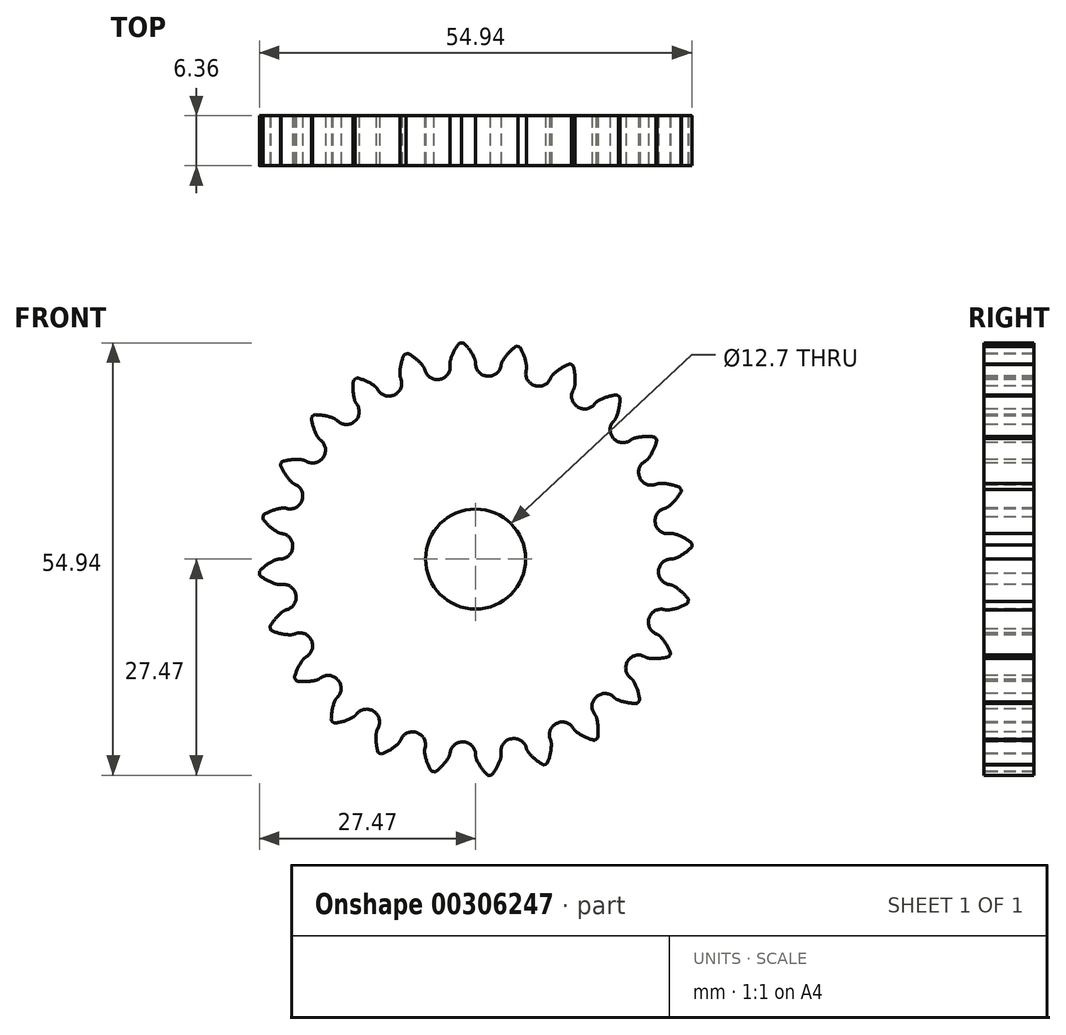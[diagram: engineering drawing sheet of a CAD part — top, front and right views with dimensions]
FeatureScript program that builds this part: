
annotation { "Feature Type Name" : "Feature", "Feature Type Description" : "" }
export const myFeature = defineFeature(function(context is Context, id is Id, definition is map)
    precondition{}
    {
        {
            var Q0;
            Q0=qCreatedBy(makeId("Front.planeOp"),FACE);
            var sketch = newSketch(context, id + "F0", { "sketchPlane" : qUnion([Q0])});
            skCircle(sketch, "E0", {"center": v(0, 0) * mm, "radius": 23.28 * mm});
            skSolve(sketch);
        }
        {
            var Q0;
            Q0=qSketchRegion(id+"F0",true);
            extrude(context, id + "F1", {"entities" : qUnion([Q0]), "depth" : 3.17 * mm});
        }
        {
            var Q0;
            Q0=makeQuery(id+"F1.opExtrude","CAP_FACE",FACE,{"disambiguationData":[OSD([sQuery(id+"F0.wireOp",EDGE,"E0")])],"isStart":true});
            extrude(context, id + "F2", {"entities" : qUnion([Q0]), "operationType" : NewBodyOperationType.ADD, "depth" : 3.17 * mm});
        }
        {
            var Q0;
            Q0=makeQuery(id+"F1.opExtrude","CAP_FACE",FACE,{"disambiguationData":[OSD([sQuery(id+"F0.wireOp",EDGE,"E0")])],"isStart":false});
            var sketch = newSketch(context, id + "F3", { "sketchPlane" : qUnion([Q0])});
            skArc(sketch, "E1.trimOffspring", {"start": v(-0.14, 25.48) * mm, "mid": v(-0.74, 26.53) * mm, "end": v(-1.53, 27.45) * mm});
            skLineSegment(sketch, "E2", {"start": v(-1.58, 27.47) * mm, "end": v(-1.8, 27.47) * mm});
            skLineSegment(sketch, "E3", {"start": v(0, 24.83) * mm, "end": v(0, 24.82) * mm});
            skLineSegment(sketch, "E4.MirrorCS", {"start": v(-2.01, 27.44) * mm, "end": v(-1.8, 27.47) * mm});
            skArc(sketch, "E5.MirrorCS", {"start": v(-3.19, 25.28) * mm, "mid": v(-2.73, 26.4) * mm, "end": v(-2.07, 27.41) * mm});
            skLineSegment(sketch, "E6.MirrorCS", {"start": v(-3.24, 24.62) * mm, "end": v(-3.24, 24.6) * mm});
            skArc(sketch, "E7.filletArc", {"start": v(-3.21, 23.06) * mm, "mid": v(-3.1, 23.13) * mm, "end": v(-3.06, 23.26) * mm});
            skArc(sketch, "E8.filletArc", {"start": v(-4.5, 22.84) * mm, "mid": v(-3.52, 23.47) * mm, "end": v(-3.24, 24.6) * mm});
            skArc(sketch, "E9.filletArc", {"start": v(0, 24.82) * mm, "mid": v(0.43, 23.73) * mm, "end": v(1.49, 23.24) * mm});
            skPoint(sketch, "E10.visualSharp", {"position": v(0, 25.15) * mm});
            skArc(sketch, "E10.filletArc", {"start": v(0, 24.83) * mm, "mid": v(-0.04, 25.16) * mm, "end": v(-0.14, 25.48) * mm});
            skPoint(sketch, "E11.visualSharp", {"position": v(-3.28, 24.93) * mm});
            skArc(sketch, "E11.filletArc", {"start": v(-3.19, 25.28) * mm, "mid": v(-3.25, 24.95) * mm, "end": v(-3.24, 24.62) * mm});
            skPoint(sketch, "E12.visualSharp", {"position": v(-2.05, 27.44) * mm});
            skArc(sketch, "E13.filletArc", {"start": v(-2.01, 27.44) * mm, "mid": v(-2.04, 27.43) * mm, "end": v(-2.07, 27.41) * mm});
            skPoint(sketch, "E14.visualSharp", {"position": v(-1.55, 27.47) * mm});
            skArc(sketch, "E14.filletArc", {"start": v(-1.53, 27.45) * mm, "mid": v(-1.55, 27.47) * mm, "end": v(-1.58, 27.47) * mm});
            skArc(sketch, "E15.1.0", {"start": v(-9.62, 23.6) * mm, "mid": v(-9.47, 24.8) * mm, "end": v(-9.1, 25.94) * mm});
            skArc(sketch, "E15.1.1", {"start": v(-6.42, 23.97) * mm, "mid": v(-5.73, 23.04) * mm, "end": v(-4.58, 22.83) * mm});
            skArc(sketch, "E15.1.2", {"start": v(-6.73, 24.58) * mm, "mid": v(-7.58, 25.44) * mm, "end": v(-8.58, 26.12) * mm});
            skPoint(sketch, "E15.1.3", {"position": v(-6.5, 24.29) * mm});
            skPoint(sketch, "E15.1.4", {"position": v(-9.62, 23.23) * mm});
            skPoint(sketch, "E15.1.5", {"position": v(-9.08, 25.98) * mm});
            skPoint(sketch, "E15.1.6", {"position": v(-8.6, 26.14) * mm});
            skArc(sketch, "E15.1.7", {"start": v(-10.27, 20.9) * mm, "mid": v(-9.48, 21.76) * mm, "end": v(-9.5, 22.93) * mm});
            skArc(sketch, "E15.1.8", {"start": v(-9.07, 21.44) * mm, "mid": v(-8.98, 21.54) * mm, "end": v(-8.98, 21.67) * mm});
            skArc(sketch, "E15.1.9", {"start": v(-6.43, 23.98) * mm, "mid": v(-6.55, 24.3) * mm, "end": v(-6.73, 24.58) * mm});
            skArc(sketch, "E15.1.10", {"start": v(-9.62, 23.6) * mm, "mid": v(-9.6, 23.26) * mm, "end": v(-9.5, 22.94) * mm});
            skLineSegment(sketch, "E15.1.11", {"start": v(-9.5, 22.94) * mm, "end": v(-9.5, 22.93) * mm});
            skLineSegment(sketch, "E15.1.12", {"start": v(-6.43, 23.98) * mm, "end": v(-6.42, 23.97) * mm});
            skLineSegment(sketch, "E15.1.13", {"start": v(-9.05, 25.99) * mm, "end": v(-8.85, 26.07) * mm});
            skArc(sketch, "E15.1.14", {"start": v(-9.05, 25.99) * mm, "mid": v(-9.08, 25.97) * mm, "end": v(-9.1, 25.94) * mm});
            skArc(sketch, "E15.1.15", {"start": v(-8.58, 26.12) * mm, "mid": v(-8.6, 26.13) * mm, "end": v(-8.64, 26.13) * mm});
            skLineSegment(sketch, "E15.1.16", {"start": v(-8.64, 26.13) * mm, "end": v(-8.85, 26.07) * mm});
            skArc(sketch, "E15.2.0", {"start": v(-15.4, 20.3) * mm, "mid": v(-15.57, 21.5) * mm, "end": v(-15.5, 22.7) * mm});
            skArc(sketch, "E15.2.1", {"start": v(-12.41, 21.5) * mm, "mid": v(-11.5, 20.77) * mm, "end": v(-10.33, 20.87) * mm});
            skArc(sketch, "E15.2.2", {"start": v(-12.86, 22) * mm, "mid": v(-13.9, 22.6) * mm, "end": v(-15.05, 23) * mm});
            skPoint(sketch, "E15.2.3", {"position": v(-12.57, 21.78) * mm});
            skPoint(sketch, "E15.2.4", {"position": v(-15.3, 19.95) * mm});
            skPoint(sketch, "E15.2.5", {"position": v(-15.5, 22.74) * mm});
            skPoint(sketch, "E15.2.6", {"position": v(-15.08, 23.02) * mm});
            skArc(sketch, "E15.2.7", {"start": v(-15.32, 17.53) * mm, "mid": v(-14.79, 18.57) * mm, "end": v(-15.1, 19.7) * mm});
            skArc(sketch, "E15.2.8", {"start": v(-14.31, 18.36) * mm, "mid": v(-14.25, 18.48) * mm, "end": v(-14.28, 18.61) * mm});
            skArc(sketch, "E15.2.9", {"start": v(-12.42, 21.5) * mm, "mid": v(-12.61, 21.77) * mm, "end": v(-12.86, 22) * mm});
            skArc(sketch, "E15.2.10", {"start": v(-15.4, 20.3) * mm, "mid": v(-15.3, 19.99) * mm, "end": v(-15.12, 19.7) * mm});
            skLineSegment(sketch, "E15.2.11", {"start": v(-15.12, 19.7) * mm, "end": v(-15.1, 19.7) * mm});
            skLineSegment(sketch, "E15.2.12", {"start": v(-12.42, 21.5) * mm, "end": v(-12.41, 21.5) * mm});
            skLineSegment(sketch, "E15.2.13", {"start": v(-15.47, 22.76) * mm, "end": v(-15.3, 22.9) * mm});
            skArc(sketch, "E15.2.14", {"start": v(-15.47, 22.76) * mm, "mid": v(-15.49, 22.74) * mm, "end": v(-15.5, 22.7) * mm});
            skArc(sketch, "E15.2.15", {"start": v(-15.05, 23) * mm, "mid": v(-15.08, 23.01) * mm, "end": v(-15.1, 23) * mm});
            skLineSegment(sketch, "E15.2.16", {"start": v(-15.1, 23) * mm, "end": v(-15.3, 22.9) * mm});
            skPoint(sketch, "E15.center", {"position": v(0, 0) * mm});
            skArc(sketch, "E16.4.3.0", {"start": v(-17.55, 17.55) * mm, "mid": v(-16.48, 17.09) * mm, "end": v(-15.38, 17.48) * mm});
            skArc(sketch, "E16.8.3.0", {"start": v(-18.12, 17.92) * mm, "mid": v(-19.29, 18.24) * mm, "end": v(-20.5, 18.33) * mm});
            skArc(sketch, "E16.9.3.0", {"start": v(-20.13, 15.62) * mm, "mid": v(-20.6, 16.74) * mm, "end": v(-20.85, 17.92) * mm});
            skPoint(sketch, "E16.12.3.0", {"position": v(-17.78, 17.78) * mm});
            skPoint(sketch, "E16.13.3.0", {"position": v(-19.95, 15.3) * mm});
            skPoint(sketch, "E16.14.3.0", {"position": v(-20.85, 17.96) * mm});
            skPoint(sketch, "E16.15.3.0", {"position": v(-20.52, 18.33) * mm});
            skArc(sketch, "E16.16.3.0", {"start": v(-19.34, 12.97) * mm, "mid": v(-19.1, 14.1) * mm, "end": v(-19.7, 15.1) * mm});
            skArc(sketch, "E16.20.3.0", {"start": v(-18.58, 14.03) * mm, "mid": v(-18.54, 14.16) * mm, "end": v(-18.61, 14.28) * mm});
            skArc(sketch, "E16.24.3.0", {"start": v(-17.56, 17.56) * mm, "mid": v(-17.82, 17.77) * mm, "end": v(-18.12, 17.92) * mm});
            skArc(sketch, "E16.28.3.0", {"start": v(-20.13, 15.62) * mm, "mid": v(-19.94, 15.35) * mm, "end": v(-19.7, 15.12) * mm});
            skLineSegment(sketch, "E16.32.3.0", {"start": v(-19.7, 15.12) * mm, "end": v(-19.7, 15.1) * mm});
            skLineSegment(sketch, "E16.35.3.0", {"start": v(-17.56, 17.56) * mm, "end": v(-17.55, 17.55) * mm});
            skLineSegment(sketch, "E16.38.3.0", {"start": v(-20.83, 17.98) * mm, "end": v(-20.7, 18.15) * mm});
            skArc(sketch, "E16.41.3.0", {"start": v(-20.83, 17.98) * mm, "mid": v(-20.85, 17.95) * mm, "end": v(-20.85, 17.92) * mm});
            skArc(sketch, "E16.45.3.0", {"start": v(-20.5, 18.33) * mm, "mid": v(-20.52, 18.32) * mm, "end": v(-20.54, 18.3) * mm});
            skLineSegment(sketch, "E16.49.3.0", {"start": v(-20.54, 18.3) * mm, "end": v(-20.7, 18.15) * mm});
            skArc(sketch, "E16.4.4.0", {"start": v(-21.5, 12.41) * mm, "mid": v(-20.34, 12.24) * mm, "end": v(-19.38, 12.9) * mm});
            skArc(sketch, "E16.8.4.0", {"start": v(-22.14, 12.62) * mm, "mid": v(-23.35, 12.63) * mm, "end": v(-24.54, 12.4) * mm});
            skArc(sketch, "E16.9.4.0", {"start": v(-23.49, 9.88) * mm, "mid": v(-24.23, 10.84) * mm, "end": v(-24.78, 11.92) * mm});
            skPoint(sketch, "E16.12.4.0", {"position": v(-21.78, 12.57) * mm});
            skPoint(sketch, "E16.13.4.0", {"position": v(-23.23, 9.62) * mm});
            skPoint(sketch, "E16.14.4.0", {"position": v(-24.79, 11.95) * mm});
            skPoint(sketch, "E16.15.4.0", {"position": v(-24.57, 12.4) * mm});
            skArc(sketch, "E16.16.4.0", {"start": v(-22.04, 7.52) * mm, "mid": v(-22.1, 8.69) * mm, "end": v(-22.93, 9.5) * mm});
            skArc(sketch, "E16.20.4.0", {"start": v(-21.58, 8.75) * mm, "mid": v(-21.58, 8.88) * mm, "end": v(-21.67, 8.98) * mm});
            skArc(sketch, "E16.24.4.0", {"start": v(-21.5, 12.42) * mm, "mid": v(-21.81, 12.55) * mm, "end": v(-22.14, 12.62) * mm});
            skArc(sketch, "E16.28.4.0", {"start": v(-23.49, 9.88) * mm, "mid": v(-23.23, 9.66) * mm, "end": v(-22.94, 9.5) * mm});
            skLineSegment(sketch, "E16.32.4.0", {"start": v(-22.94, 9.5) * mm, "end": v(-22.93, 9.5) * mm});
            skLineSegment(sketch, "E16.35.4.0", {"start": v(-21.5, 12.42) * mm, "end": v(-21.5, 12.41) * mm});
            skLineSegment(sketch, "E16.38.4.0", {"start": v(-24.78, 11.98) * mm, "end": v(-24.7, 12.18) * mm});
            skArc(sketch, "E16.41.4.0", {"start": v(-24.78, 11.98) * mm, "mid": v(-24.78, 11.95) * mm, "end": v(-24.78, 11.92) * mm});
            skArc(sketch, "E16.45.4.0", {"start": v(-24.54, 12.4) * mm, "mid": v(-24.56, 12.39) * mm, "end": v(-24.58, 12.37) * mm});
            skLineSegment(sketch, "E16.49.4.0", {"start": v(-24.58, 12.37) * mm, "end": v(-24.7, 12.18) * mm});
            skArc(sketch, "E16.4.5.0", {"start": v(-23.97, 6.42) * mm, "mid": v(-22.81, 6.56) * mm, "end": v(-22.06, 7.45) * mm});
            skArc(sketch, "E16.8.5.0", {"start": v(-24.65, 6.46) * mm, "mid": v(-25.82, 6.15) * mm, "end": v(-26.91, 5.63) * mm});
            skArc(sketch, "E16.9.5.0", {"start": v(-25.25, 3.47) * mm, "mid": v(-26.2, 4.2) * mm, "end": v(-27.02, 5.1) * mm});
            skPoint(sketch, "E16.12.5.0", {"position": v(-24.29, 6.5) * mm});
            skPoint(sketch, "E16.13.5.0", {"position": v(-24.93, 3.28) * mm});
            skPoint(sketch, "E16.14.5.0", {"position": v(-27.04, 5.12) * mm});
            skPoint(sketch, "E16.15.5.0", {"position": v(-26.94, 5.61) * mm});
            skArc(sketch, "E16.16.5.0", {"start": v(-23.23, 1.56) * mm, "mid": v(-23.59, 2.67) * mm, "end": v(-24.6, 3.24) * mm});
            skArc(sketch, "E16.20.5.0", {"start": v(-23.1, 2.86) * mm, "mid": v(-23.14, 3) * mm, "end": v(-23.26, 3.06) * mm});
            skArc(sketch, "E16.24.5.0", {"start": v(-23.98, 6.43) * mm, "mid": v(-24.32, 6.48) * mm, "end": v(-24.65, 6.46) * mm});
            skArc(sketch, "E16.28.5.0", {"start": v(-25.25, 3.47) * mm, "mid": v(-24.94, 3.32) * mm, "end": v(-24.62, 3.24) * mm});
            skLineSegment(sketch, "E16.32.5.0", {"start": v(-24.62, 3.24) * mm, "end": v(-24.6, 3.24) * mm});
            skLineSegment(sketch, "E16.35.5.0", {"start": v(-23.98, 6.43) * mm, "end": v(-23.97, 6.42) * mm});
            skLineSegment(sketch, "E16.38.5.0", {"start": v(-27.03, 5.16) * mm, "end": v(-27, 5.37) * mm});
            skArc(sketch, "E16.41.5.0", {"start": v(-27.03, 5.16) * mm, "mid": v(-27.03, 5.13) * mm, "end": v(-27.02, 5.1) * mm});
            skArc(sketch, "E16.45.5.0", {"start": v(-26.91, 5.63) * mm, "mid": v(-26.93, 5.6) * mm, "end": v(-26.95, 5.58) * mm});
            skLineSegment(sketch, "E16.49.5.0", {"start": v(-26.95, 5.58) * mm, "end": v(-27, 5.37) * mm});
            skArc(sketch, "E16.4.6.0", {"start": v(-24.82, 0) * mm, "mid": v(-23.73, 0.43) * mm, "end": v(-23.24, 1.49) * mm});
            skArc(sketch, "E16.8.6.0", {"start": v(-25.48, -0.14) * mm, "mid": v(-26.53, -0.74) * mm, "end": v(-27.45, -1.53) * mm});
            skArc(sketch, "E16.9.6.0", {"start": v(-25.28, -3.19) * mm, "mid": v(-26.4, -2.73) * mm, "end": v(-27.41, -2.07) * mm});
            skPoint(sketch, "E16.12.6.0", {"position": v(-25.15, 0) * mm});
            skPoint(sketch, "E16.13.6.0", {"position": v(-24.93, -3.28) * mm});
            skPoint(sketch, "E16.14.6.0", {"position": v(-27.44, -2.05) * mm});
            skPoint(sketch, "E16.15.6.0", {"position": v(-27.47, -1.55) * mm});
            skArc(sketch, "E16.16.6.0", {"start": v(-22.84, -4.5) * mm, "mid": v(-23.47, -3.52) * mm, "end": v(-24.6, -3.24) * mm});
            skArc(sketch, "E16.20.6.0", {"start": v(-23.06, -3.21) * mm, "mid": v(-23.13, -3.1) * mm, "end": v(-23.26, -3.06) * mm});
            skArc(sketch, "E16.24.6.0", {"start": v(-24.83, 0) * mm, "mid": v(-25.16, -0.04) * mm, "end": v(-25.48, -0.14) * mm});
            skArc(sketch, "E16.28.6.0", {"start": v(-25.28, -3.19) * mm, "mid": v(-24.95, -3.25) * mm, "end": v(-24.62, -3.24) * mm});
            skLineSegment(sketch, "E16.32.6.0", {"start": v(-24.62, -3.24) * mm, "end": v(-24.6, -3.24) * mm});
            skLineSegment(sketch, "E16.35.6.0", {"start": v(-24.83, 0) * mm, "end": v(-24.82, 0) * mm});
            skLineSegment(sketch, "E16.38.6.0", {"start": v(-27.44, -2.01) * mm, "end": v(-27.47, -1.8) * mm});
            skArc(sketch, "E16.41.6.0", {"start": v(-27.44, -2.01) * mm, "mid": v(-27.43, -2.04) * mm, "end": v(-27.41, -2.07) * mm});
            skArc(sketch, "E16.45.6.0", {"start": v(-27.45, -1.53) * mm, "mid": v(-27.47, -1.55) * mm, "end": v(-27.47, -1.58) * mm});
            skLineSegment(sketch, "E16.49.6.0", {"start": v(-27.47, -1.58) * mm, "end": v(-27.47, -1.8) * mm});
            skArc(sketch, "E16.4.7.0", {"start": v(-23.97, -6.42) * mm, "mid": v(-23.04, -5.73) * mm, "end": v(-22.83, -4.58) * mm});
            skArc(sketch, "E16.8.7.0", {"start": v(-24.58, -6.73) * mm, "mid": v(-25.44, -7.58) * mm, "end": v(-26.12, -8.58) * mm});
            skArc(sketch, "E16.9.7.0", {"start": v(-23.6, -9.62) * mm, "mid": v(-24.8, -9.47) * mm, "end": v(-25.94, -9.1) * mm});
            skPoint(sketch, "E16.12.7.0", {"position": v(-24.29, -6.5) * mm});
            skPoint(sketch, "E16.13.7.0", {"position": v(-23.23, -9.62) * mm});
            skPoint(sketch, "E16.14.7.0", {"position": v(-25.98, -9.08) * mm});
            skPoint(sketch, "E16.15.7.0", {"position": v(-26.14, -8.6) * mm});
            skArc(sketch, "E16.16.7.0", {"start": v(-20.9, -10.27) * mm, "mid": v(-21.76, -9.48) * mm, "end": v(-22.93, -9.5) * mm});
            skArc(sketch, "E16.20.7.0", {"start": v(-21.44, -9.07) * mm, "mid": v(-21.54, -8.98) * mm, "end": v(-21.67, -8.98) * mm});
            skArc(sketch, "E16.24.7.0", {"start": v(-23.98, -6.43) * mm, "mid": v(-24.3, -6.55) * mm, "end": v(-24.58, -6.73) * mm});
            skArc(sketch, "E16.28.7.0", {"start": v(-23.6, -9.62) * mm, "mid": v(-23.26, -9.6) * mm, "end": v(-22.94, -9.5) * mm});
            skLineSegment(sketch, "E16.32.7.0", {"start": v(-22.94, -9.5) * mm, "end": v(-22.93, -9.5) * mm});
            skLineSegment(sketch, "E16.35.7.0", {"start": v(-23.98, -6.43) * mm, "end": v(-23.97, -6.42) * mm});
            skLineSegment(sketch, "E16.38.7.0", {"start": v(-25.99, -9.05) * mm, "end": v(-26.07, -8.85) * mm});
            skArc(sketch, "E16.41.7.0", {"start": v(-25.99, -9.05) * mm, "mid": v(-25.97, -9.08) * mm, "end": v(-25.94, -9.1) * mm});
            skArc(sketch, "E16.45.7.0", {"start": v(-26.12, -8.58) * mm, "mid": v(-26.13, -8.6) * mm, "end": v(-26.13, -8.64) * mm});
            skLineSegment(sketch, "E16.49.7.0", {"start": v(-26.13, -8.64) * mm, "end": v(-26.07, -8.85) * mm});
            skArc(sketch, "E16.4.8.0", {"start": v(-21.5, -12.41) * mm, "mid": v(-20.77, -11.5) * mm, "end": v(-20.87, -10.33) * mm});
            skArc(sketch, "E16.8.8.0", {"start": v(-22, -12.86) * mm, "mid": v(-22.6, -13.9) * mm, "end": v(-23, -15.05) * mm});
            skArc(sketch, "E16.9.8.0", {"start": v(-20.3, -15.4) * mm, "mid": v(-21.5, -15.57) * mm, "end": v(-22.7, -15.5) * mm});
            skPoint(sketch, "E16.12.8.0", {"position": v(-21.78, -12.57) * mm});
            skPoint(sketch, "E16.13.8.0", {"position": v(-19.95, -15.3) * mm});
            skPoint(sketch, "E16.14.8.0", {"position": v(-22.74, -15.5) * mm});
            skPoint(sketch, "E16.15.8.0", {"position": v(-23.02, -15.08) * mm});
            skArc(sketch, "E16.16.8.0", {"start": v(-17.53, -15.32) * mm, "mid": v(-18.57, -14.79) * mm, "end": v(-19.7, -15.1) * mm});
            skArc(sketch, "E16.20.8.0", {"start": v(-18.36, -14.31) * mm, "mid": v(-18.48, -14.25) * mm, "end": v(-18.61, -14.28) * mm});
            skArc(sketch, "E16.24.8.0", {"start": v(-21.5, -12.42) * mm, "mid": v(-21.77, -12.61) * mm, "end": v(-22, -12.86) * mm});
            skArc(sketch, "E16.28.8.0", {"start": v(-20.3, -15.4) * mm, "mid": v(-19.99, -15.3) * mm, "end": v(-19.7, -15.12) * mm});
            skLineSegment(sketch, "E16.32.8.0", {"start": v(-19.7, -15.12) * mm, "end": v(-19.7, -15.1) * mm});
            skLineSegment(sketch, "E16.35.8.0", {"start": v(-21.5, -12.42) * mm, "end": v(-21.5, -12.41) * mm});
            skLineSegment(sketch, "E16.38.8.0", {"start": v(-22.76, -15.47) * mm, "end": v(-22.9, -15.3) * mm});
            skArc(sketch, "E16.41.8.0", {"start": v(-22.76, -15.47) * mm, "mid": v(-22.74, -15.49) * mm, "end": v(-22.7, -15.5) * mm});
            skArc(sketch, "E16.45.8.0", {"start": v(-23, -15.05) * mm, "mid": v(-23.01, -15.08) * mm, "end": v(-23, -15.1) * mm});
            skLineSegment(sketch, "E16.49.8.0", {"start": v(-23, -15.1) * mm, "end": v(-22.9, -15.3) * mm});
            skArc(sketch, "E16.4.9.0", {"start": v(-17.55, -17.55) * mm, "mid": v(-17.09, -16.48) * mm, "end": v(-17.48, -15.38) * mm});
            skArc(sketch, "E16.8.9.0", {"start": v(-17.92, -18.12) * mm, "mid": v(-18.24, -19.29) * mm, "end": v(-18.33, -20.5) * mm});
            skArc(sketch, "E16.9.9.0", {"start": v(-15.62, -20.13) * mm, "mid": v(-16.74, -20.6) * mm, "end": v(-17.92, -20.85) * mm});
            skPoint(sketch, "E16.12.9.0", {"position": v(-17.78, -17.78) * mm});
            skPoint(sketch, "E16.13.9.0", {"position": v(-15.3, -19.95) * mm});
            skPoint(sketch, "E16.14.9.0", {"position": v(-17.96, -20.85) * mm});
            skPoint(sketch, "E16.15.9.0", {"position": v(-18.33, -20.52) * mm});
            skArc(sketch, "E16.16.9.0", {"start": v(-12.97, -19.34) * mm, "mid": v(-14.1, -19.1) * mm, "end": v(-15.1, -19.7) * mm});
            skArc(sketch, "E16.20.9.0", {"start": v(-14.03, -18.58) * mm, "mid": v(-14.16, -18.54) * mm, "end": v(-14.28, -18.61) * mm});
            skArc(sketch, "E16.24.9.0", {"start": v(-17.56, -17.56) * mm, "mid": v(-17.77, -17.82) * mm, "end": v(-17.92, -18.12) * mm});
            skArc(sketch, "E16.28.9.0", {"start": v(-15.62, -20.13) * mm, "mid": v(-15.35, -19.94) * mm, "end": v(-15.12, -19.7) * mm});
            skLineSegment(sketch, "E16.32.9.0", {"start": v(-15.12, -19.7) * mm, "end": v(-15.1, -19.7) * mm});
            skLineSegment(sketch, "E16.35.9.0", {"start": v(-17.56, -17.56) * mm, "end": v(-17.55, -17.55) * mm});
            skLineSegment(sketch, "E16.38.9.0", {"start": v(-17.98, -20.83) * mm, "end": v(-18.15, -20.7) * mm});
            skArc(sketch, "E16.41.9.0", {"start": v(-17.98, -20.83) * mm, "mid": v(-17.95, -20.85) * mm, "end": v(-17.92, -20.85) * mm});
            skArc(sketch, "E16.45.9.0", {"start": v(-18.33, -20.5) * mm, "mid": v(-18.32, -20.52) * mm, "end": v(-18.3, -20.54) * mm});
            skLineSegment(sketch, "E16.49.9.0", {"start": v(-18.3, -20.54) * mm, "end": v(-18.15, -20.7) * mm});
            skArc(sketch, "E16.4.10.0", {"start": v(-12.41, -21.5) * mm, "mid": v(-12.24, -20.34) * mm, "end": v(-12.9, -19.38) * mm});
            skArc(sketch, "E16.8.10.0", {"start": v(-12.62, -22.14) * mm, "mid": v(-12.63, -23.35) * mm, "end": v(-12.4, -24.54) * mm});
            skArc(sketch, "E16.9.10.0", {"start": v(-9.88, -23.49) * mm, "mid": v(-10.84, -24.23) * mm, "end": v(-11.92, -24.78) * mm});
            skPoint(sketch, "E16.12.10.0", {"position": v(-12.57, -21.78) * mm});
            skPoint(sketch, "E16.13.10.0", {"position": v(-9.62, -23.23) * mm});
            skPoint(sketch, "E16.14.10.0", {"position": v(-11.95, -24.79) * mm});
            skPoint(sketch, "E16.15.10.0", {"position": v(-12.4, -24.57) * mm});
            skArc(sketch, "E16.16.10.0", {"start": v(-7.52, -22.04) * mm, "mid": v(-8.69, -22.1) * mm, "end": v(-9.5, -22.93) * mm});
            skArc(sketch, "E16.20.10.0", {"start": v(-8.75, -21.58) * mm, "mid": v(-8.88, -21.58) * mm, "end": v(-8.98, -21.67) * mm});
            skArc(sketch, "E16.24.10.0", {"start": v(-12.42, -21.5) * mm, "mid": v(-12.55, -21.81) * mm, "end": v(-12.62, -22.14) * mm});
            skArc(sketch, "E16.28.10.0", {"start": v(-9.88, -23.49) * mm, "mid": v(-9.66, -23.23) * mm, "end": v(-9.5, -22.94) * mm});
            skLineSegment(sketch, "E16.32.10.0", {"start": v(-9.5, -22.94) * mm, "end": v(-9.5, -22.93) * mm});
            skLineSegment(sketch, "E16.35.10.0", {"start": v(-12.42, -21.5) * mm, "end": v(-12.41, -21.5) * mm});
            skLineSegment(sketch, "E16.38.10.0", {"start": v(-11.98, -24.78) * mm, "end": v(-12.18, -24.7) * mm});
            skArc(sketch, "E16.41.10.0", {"start": v(-11.98, -24.78) * mm, "mid": v(-11.95, -24.78) * mm, "end": v(-11.92, -24.78) * mm});
            skArc(sketch, "E16.45.10.0", {"start": v(-12.4, -24.54) * mm, "mid": v(-12.39, -24.56) * mm, "end": v(-12.37, -24.58) * mm});
            skLineSegment(sketch, "E16.49.10.0", {"start": v(-12.37, -24.58) * mm, "end": v(-12.18, -24.7) * mm});
            skArc(sketch, "E16.4.11.0", {"start": v(-6.42, -23.97) * mm, "mid": v(-6.56, -22.81) * mm, "end": v(-7.45, -22.06) * mm});
            skArc(sketch, "E16.8.11.0", {"start": v(-6.46, -24.65) * mm, "mid": v(-6.15, -25.82) * mm, "end": v(-5.63, -26.91) * mm});
            skArc(sketch, "E16.9.11.0", {"start": v(-3.47, -25.25) * mm, "mid": v(-4.2, -26.2) * mm, "end": v(-5.1, -27.02) * mm});
            skPoint(sketch, "E16.12.11.0", {"position": v(-6.5, -24.29) * mm});
            skPoint(sketch, "E16.13.11.0", {"position": v(-3.28, -24.93) * mm});
            skPoint(sketch, "E16.14.11.0", {"position": v(-5.12, -27.04) * mm});
            skPoint(sketch, "E16.15.11.0", {"position": v(-5.61, -26.94) * mm});
            skArc(sketch, "E16.16.11.0", {"start": v(-1.56, -23.23) * mm, "mid": v(-2.67, -23.59) * mm, "end": v(-3.24, -24.6) * mm});
            skArc(sketch, "E16.20.11.0", {"start": v(-2.86, -23.1) * mm, "mid": v(-3, -23.14) * mm, "end": v(-3.06, -23.26) * mm});
            skArc(sketch, "E16.24.11.0", {"start": v(-6.43, -23.98) * mm, "mid": v(-6.48, -24.32) * mm, "end": v(-6.46, -24.65) * mm});
            skArc(sketch, "E16.28.11.0", {"start": v(-3.47, -25.25) * mm, "mid": v(-3.32, -24.94) * mm, "end": v(-3.24, -24.62) * mm});
            skLineSegment(sketch, "E16.32.11.0", {"start": v(-3.24, -24.62) * mm, "end": v(-3.24, -24.6) * mm});
            skLineSegment(sketch, "E16.35.11.0", {"start": v(-6.43, -23.98) * mm, "end": v(-6.42, -23.97) * mm});
            skLineSegment(sketch, "E16.38.11.0", {"start": v(-5.16, -27.03) * mm, "end": v(-5.37, -27) * mm});
            skArc(sketch, "E16.41.11.0", {"start": v(-5.16, -27.03) * mm, "mid": v(-5.13, -27.03) * mm, "end": v(-5.1, -27.02) * mm});
            skArc(sketch, "E16.45.11.0", {"start": v(-5.63, -26.91) * mm, "mid": v(-5.6, -26.93) * mm, "end": v(-5.58, -26.95) * mm});
            skLineSegment(sketch, "E16.49.11.0", {"start": v(-5.58, -26.95) * mm, "end": v(-5.37, -27) * mm});
            skArc(sketch, "E16.4.12.0", {"start": v(0, -24.82) * mm, "mid": v(-0.43, -23.73) * mm, "end": v(-1.49, -23.24) * mm});
            skArc(sketch, "E16.8.12.0", {"start": v(0.14, -25.48) * mm, "mid": v(0.74, -26.53) * mm, "end": v(1.53, -27.45) * mm});
            skArc(sketch, "E16.9.12.0", {"start": v(3.19, -25.28) * mm, "mid": v(2.73, -26.4) * mm, "end": v(2.07, -27.41) * mm});
            skPoint(sketch, "E16.12.12.0", {"position": v(0, -25.15) * mm});
            skPoint(sketch, "E16.13.12.0", {"position": v(3.28, -24.93) * mm});
            skPoint(sketch, "E16.14.12.0", {"position": v(2.05, -27.44) * mm});
            skPoint(sketch, "E16.15.12.0", {"position": v(1.55, -27.47) * mm});
            skArc(sketch, "E16.16.12.0", {"start": v(4.5, -22.84) * mm, "mid": v(3.52, -23.47) * mm, "end": v(3.24, -24.6) * mm});
            skArc(sketch, "E16.20.12.0", {"start": v(3.21, -23.06) * mm, "mid": v(3.1, -23.13) * mm, "end": v(3.06, -23.26) * mm});
            skArc(sketch, "E16.24.12.0", {"start": v(0, -24.83) * mm, "mid": v(0.04, -25.16) * mm, "end": v(0.14, -25.48) * mm});
            skArc(sketch, "E16.28.12.0", {"start": v(3.19, -25.28) * mm, "mid": v(3.25, -24.95) * mm, "end": v(3.24, -24.62) * mm});
            skLineSegment(sketch, "E16.32.12.0", {"start": v(3.24, -24.62) * mm, "end": v(3.24, -24.6) * mm});
            skLineSegment(sketch, "E16.35.12.0", {"start": v(0, -24.83) * mm, "end": v(0, -24.82) * mm});
            skLineSegment(sketch, "E16.38.12.0", {"start": v(2.01, -27.44) * mm, "end": v(1.8, -27.47) * mm});
            skArc(sketch, "E16.41.12.0", {"start": v(2.01, -27.44) * mm, "mid": v(2.04, -27.43) * mm, "end": v(2.07, -27.41) * mm});
            skArc(sketch, "E16.45.12.0", {"start": v(1.53, -27.45) * mm, "mid": v(1.55, -27.47) * mm, "end": v(1.58, -27.47) * mm});
            skLineSegment(sketch, "E16.49.12.0", {"start": v(1.58, -27.47) * mm, "end": v(1.8, -27.47) * mm});
            skArc(sketch, "E16.4.13.0", {"start": v(6.42, -23.97) * mm, "mid": v(5.73, -23.04) * mm, "end": v(4.58, -22.83) * mm});
            skArc(sketch, "E16.8.13.0", {"start": v(6.73, -24.58) * mm, "mid": v(7.58, -25.44) * mm, "end": v(8.58, -26.12) * mm});
            skArc(sketch, "E16.9.13.0", {"start": v(9.62, -23.6) * mm, "mid": v(9.47, -24.8) * mm, "end": v(9.1, -25.94) * mm});
            skPoint(sketch, "E16.12.13.0", {"position": v(6.5, -24.29) * mm});
            skPoint(sketch, "E16.13.13.0", {"position": v(9.62, -23.23) * mm});
            skPoint(sketch, "E16.14.13.0", {"position": v(9.08, -25.98) * mm});
            skPoint(sketch, "E16.15.13.0", {"position": v(8.6, -26.14) * mm});
            skArc(sketch, "E16.16.13.0", {"start": v(10.27, -20.9) * mm, "mid": v(9.48, -21.76) * mm, "end": v(9.5, -22.93) * mm});
            skArc(sketch, "E16.20.13.0", {"start": v(9.07, -21.44) * mm, "mid": v(8.98, -21.54) * mm, "end": v(8.98, -21.67) * mm});
            skArc(sketch, "E16.24.13.0", {"start": v(6.43, -23.98) * mm, "mid": v(6.55, -24.3) * mm, "end": v(6.73, -24.58) * mm});
            skArc(sketch, "E16.28.13.0", {"start": v(9.62, -23.6) * mm, "mid": v(9.6, -23.26) * mm, "end": v(9.5, -22.94) * mm});
            skLineSegment(sketch, "E16.32.13.0", {"start": v(9.5, -22.94) * mm, "end": v(9.5, -22.93) * mm});
            skLineSegment(sketch, "E16.35.13.0", {"start": v(6.43, -23.98) * mm, "end": v(6.42, -23.97) * mm});
            skLineSegment(sketch, "E16.38.13.0", {"start": v(9.05, -25.99) * mm, "end": v(8.85, -26.07) * mm});
            skArc(sketch, "E16.41.13.0", {"start": v(9.05, -25.99) * mm, "mid": v(9.08, -25.97) * mm, "end": v(9.1, -25.94) * mm});
            skArc(sketch, "E16.45.13.0", {"start": v(8.58, -26.12) * mm, "mid": v(8.6, -26.13) * mm, "end": v(8.64, -26.13) * mm});
            skLineSegment(sketch, "E16.49.13.0", {"start": v(8.64, -26.13) * mm, "end": v(8.85, -26.07) * mm});
            skArc(sketch, "E16.4.14.0", {"start": v(12.41, -21.5) * mm, "mid": v(11.5, -20.77) * mm, "end": v(10.33, -20.87) * mm});
            skArc(sketch, "E16.8.14.0", {"start": v(12.86, -22) * mm, "mid": v(13.9, -22.6) * mm, "end": v(15.05, -23) * mm});
            skArc(sketch, "E16.9.14.0", {"start": v(15.4, -20.3) * mm, "mid": v(15.57, -21.5) * mm, "end": v(15.5, -22.7) * mm});
            skPoint(sketch, "E16.12.14.0", {"position": v(12.57, -21.78) * mm});
            skPoint(sketch, "E16.13.14.0", {"position": v(15.3, -19.95) * mm});
            skPoint(sketch, "E16.14.14.0", {"position": v(15.5, -22.74) * mm});
            skPoint(sketch, "E16.15.14.0", {"position": v(15.08, -23.02) * mm});
            skArc(sketch, "E16.16.14.0", {"start": v(15.32, -17.53) * mm, "mid": v(14.79, -18.57) * mm, "end": v(15.1, -19.7) * mm});
            skArc(sketch, "E16.20.14.0", {"start": v(14.31, -18.36) * mm, "mid": v(14.25, -18.48) * mm, "end": v(14.28, -18.61) * mm});
            skArc(sketch, "E16.24.14.0", {"start": v(12.42, -21.5) * mm, "mid": v(12.61, -21.77) * mm, "end": v(12.86, -22) * mm});
            skArc(sketch, "E16.28.14.0", {"start": v(15.4, -20.3) * mm, "mid": v(15.3, -19.99) * mm, "end": v(15.12, -19.7) * mm});
            skLineSegment(sketch, "E16.32.14.0", {"start": v(15.12, -19.7) * mm, "end": v(15.1, -19.7) * mm});
            skLineSegment(sketch, "E16.35.14.0", {"start": v(12.42, -21.5) * mm, "end": v(12.41, -21.5) * mm});
            skLineSegment(sketch, "E16.38.14.0", {"start": v(15.47, -22.76) * mm, "end": v(15.3, -22.9) * mm});
            skArc(sketch, "E16.41.14.0", {"start": v(15.47, -22.76) * mm, "mid": v(15.49, -22.74) * mm, "end": v(15.5, -22.7) * mm});
            skArc(sketch, "E16.45.14.0", {"start": v(15.05, -23) * mm, "mid": v(15.08, -23.01) * mm, "end": v(15.1, -23) * mm});
            skLineSegment(sketch, "E16.49.14.0", {"start": v(15.1, -23) * mm, "end": v(15.3, -22.9) * mm});
            skArc(sketch, "E16.4.15.0", {"start": v(17.55, -17.55) * mm, "mid": v(16.48, -17.09) * mm, "end": v(15.38, -17.48) * mm});
            skArc(sketch, "E16.8.15.0", {"start": v(18.12, -17.92) * mm, "mid": v(19.29, -18.24) * mm, "end": v(20.5, -18.33) * mm});
            skArc(sketch, "E16.9.15.0", {"start": v(20.13, -15.62) * mm, "mid": v(20.6, -16.74) * mm, "end": v(20.85, -17.92) * mm});
            skPoint(sketch, "E16.12.15.0", {"position": v(17.78, -17.78) * mm});
            skPoint(sketch, "E16.13.15.0", {"position": v(19.95, -15.3) * mm});
            skPoint(sketch, "E16.14.15.0", {"position": v(20.85, -17.96) * mm});
            skPoint(sketch, "E16.15.15.0", {"position": v(20.52, -18.33) * mm});
            skArc(sketch, "E16.16.15.0", {"start": v(19.34, -12.97) * mm, "mid": v(19.1, -14.1) * mm, "end": v(19.7, -15.1) * mm});
            skArc(sketch, "E16.20.15.0", {"start": v(18.58, -14.03) * mm, "mid": v(18.54, -14.16) * mm, "end": v(18.61, -14.28) * mm});
            skArc(sketch, "E16.24.15.0", {"start": v(17.56, -17.56) * mm, "mid": v(17.82, -17.77) * mm, "end": v(18.12, -17.92) * mm});
            skArc(sketch, "E16.28.15.0", {"start": v(20.13, -15.62) * mm, "mid": v(19.94, -15.35) * mm, "end": v(19.7, -15.12) * mm});
            skLineSegment(sketch, "E16.32.15.0", {"start": v(19.7, -15.12) * mm, "end": v(19.7, -15.1) * mm});
            skLineSegment(sketch, "E16.35.15.0", {"start": v(17.56, -17.56) * mm, "end": v(17.55, -17.55) * mm});
            skLineSegment(sketch, "E16.38.15.0", {"start": v(20.83, -17.98) * mm, "end": v(20.7, -18.15) * mm});
            skArc(sketch, "E16.41.15.0", {"start": v(20.83, -17.98) * mm, "mid": v(20.85, -17.95) * mm, "end": v(20.85, -17.92) * mm});
            skArc(sketch, "E16.45.15.0", {"start": v(20.5, -18.33) * mm, "mid": v(20.52, -18.32) * mm, "end": v(20.54, -18.3) * mm});
            skLineSegment(sketch, "E16.49.15.0", {"start": v(20.54, -18.3) * mm, "end": v(20.7, -18.15) * mm});
            skArc(sketch, "E16.4.16.0", {"start": v(21.5, -12.41) * mm, "mid": v(20.34, -12.24) * mm, "end": v(19.38, -12.9) * mm});
            skArc(sketch, "E16.8.16.0", {"start": v(22.14, -12.62) * mm, "mid": v(23.35, -12.63) * mm, "end": v(24.54, -12.4) * mm});
            skArc(sketch, "E16.9.16.0", {"start": v(23.49, -9.88) * mm, "mid": v(24.23, -10.84) * mm, "end": v(24.78, -11.92) * mm});
            skPoint(sketch, "E16.12.16.0", {"position": v(21.78, -12.57) * mm});
            skPoint(sketch, "E16.13.16.0", {"position": v(23.23, -9.62) * mm});
            skPoint(sketch, "E16.14.16.0", {"position": v(24.79, -11.95) * mm});
            skPoint(sketch, "E16.15.16.0", {"position": v(24.57, -12.4) * mm});
            skArc(sketch, "E16.16.16.0", {"start": v(22.04, -7.52) * mm, "mid": v(22.1, -8.69) * mm, "end": v(22.93, -9.5) * mm});
            skArc(sketch, "E16.20.16.0", {"start": v(21.58, -8.75) * mm, "mid": v(21.58, -8.88) * mm, "end": v(21.67, -8.98) * mm});
            skArc(sketch, "E16.24.16.0", {"start": v(21.5, -12.42) * mm, "mid": v(21.81, -12.55) * mm, "end": v(22.14, -12.62) * mm});
            skArc(sketch, "E16.28.16.0", {"start": v(23.49, -9.88) * mm, "mid": v(23.23, -9.66) * mm, "end": v(22.94, -9.5) * mm});
            skLineSegment(sketch, "E16.32.16.0", {"start": v(22.94, -9.5) * mm, "end": v(22.93, -9.5) * mm});
            skLineSegment(sketch, "E16.35.16.0", {"start": v(21.5, -12.42) * mm, "end": v(21.5, -12.41) * mm});
            skLineSegment(sketch, "E16.38.16.0", {"start": v(24.78, -11.98) * mm, "end": v(24.7, -12.18) * mm});
            skArc(sketch, "E16.41.16.0", {"start": v(24.78, -11.98) * mm, "mid": v(24.78, -11.95) * mm, "end": v(24.78, -11.92) * mm});
            skArc(sketch, "E16.45.16.0", {"start": v(24.54, -12.4) * mm, "mid": v(24.56, -12.39) * mm, "end": v(24.58, -12.37) * mm});
            skLineSegment(sketch, "E16.49.16.0", {"start": v(24.58, -12.37) * mm, "end": v(24.7, -12.18) * mm});
            skArc(sketch, "E16.4.17.0", {"start": v(23.97, -6.42) * mm, "mid": v(22.81, -6.56) * mm, "end": v(22.06, -7.45) * mm});
            skArc(sketch, "E16.8.17.0", {"start": v(24.65, -6.46) * mm, "mid": v(25.82, -6.15) * mm, "end": v(26.91, -5.63) * mm});
            skArc(sketch, "E16.9.17.0", {"start": v(25.25, -3.47) * mm, "mid": v(26.2, -4.2) * mm, "end": v(27.02, -5.1) * mm});
            skPoint(sketch, "E16.12.17.0", {"position": v(24.29, -6.5) * mm});
            skPoint(sketch, "E16.13.17.0", {"position": v(24.93, -3.28) * mm});
            skPoint(sketch, "E16.14.17.0", {"position": v(27.04, -5.12) * mm});
            skPoint(sketch, "E16.15.17.0", {"position": v(26.94, -5.61) * mm});
            skArc(sketch, "E16.16.17.0", {"start": v(23.23, -1.56) * mm, "mid": v(23.59, -2.67) * mm, "end": v(24.6, -3.24) * mm});
            skArc(sketch, "E16.20.17.0", {"start": v(23.1, -2.86) * mm, "mid": v(23.14, -3) * mm, "end": v(23.26, -3.06) * mm});
            skArc(sketch, "E16.24.17.0", {"start": v(23.98, -6.43) * mm, "mid": v(24.32, -6.48) * mm, "end": v(24.65, -6.46) * mm});
            skArc(sketch, "E16.28.17.0", {"start": v(25.25, -3.47) * mm, "mid": v(24.94, -3.32) * mm, "end": v(24.62, -3.24) * mm});
            skLineSegment(sketch, "E16.32.17.0", {"start": v(24.62, -3.24) * mm, "end": v(24.6, -3.24) * mm});
            skLineSegment(sketch, "E16.35.17.0", {"start": v(23.98, -6.43) * mm, "end": v(23.97, -6.42) * mm});
            skLineSegment(sketch, "E16.38.17.0", {"start": v(27.03, -5.16) * mm, "end": v(27, -5.37) * mm});
            skArc(sketch, "E16.41.17.0", {"start": v(27.03, -5.16) * mm, "mid": v(27.03, -5.13) * mm, "end": v(27.02, -5.1) * mm});
            skArc(sketch, "E16.45.17.0", {"start": v(26.91, -5.63) * mm, "mid": v(26.93, -5.6) * mm, "end": v(26.95, -5.58) * mm});
            skLineSegment(sketch, "E16.49.17.0", {"start": v(26.95, -5.58) * mm, "end": v(27, -5.37) * mm});
            skArc(sketch, "E16.4.18.0", {"start": v(24.82, 0) * mm, "mid": v(23.73, -0.43) * mm, "end": v(23.24, -1.49) * mm});
            skArc(sketch, "E16.8.18.0", {"start": v(25.48, 0.14) * mm, "mid": v(26.53, 0.74) * mm, "end": v(27.45, 1.53) * mm});
            skArc(sketch, "E16.9.18.0", {"start": v(25.28, 3.19) * mm, "mid": v(26.4, 2.73) * mm, "end": v(27.41, 2.07) * mm});
            skPoint(sketch, "E16.12.18.0", {"position": v(25.15, 0) * mm});
            skPoint(sketch, "E16.13.18.0", {"position": v(24.93, 3.28) * mm});
            skPoint(sketch, "E16.14.18.0", {"position": v(27.44, 2.05) * mm});
            skPoint(sketch, "E16.15.18.0", {"position": v(27.47, 1.55) * mm});
            skArc(sketch, "E16.16.18.0", {"start": v(22.84, 4.5) * mm, "mid": v(23.47, 3.52) * mm, "end": v(24.6, 3.24) * mm});
            skArc(sketch, "E16.20.18.0", {"start": v(23.06, 3.21) * mm, "mid": v(23.13, 3.1) * mm, "end": v(23.26, 3.06) * mm});
            skArc(sketch, "E16.24.18.0", {"start": v(24.83, 0) * mm, "mid": v(25.16, 0.04) * mm, "end": v(25.48, 0.14) * mm});
            skArc(sketch, "E16.28.18.0", {"start": v(25.28, 3.19) * mm, "mid": v(24.95, 3.25) * mm, "end": v(24.62, 3.24) * mm});
            skLineSegment(sketch, "E16.32.18.0", {"start": v(24.62, 3.24) * mm, "end": v(24.6, 3.24) * mm});
            skLineSegment(sketch, "E16.35.18.0", {"start": v(24.83, 0) * mm, "end": v(24.82, 0) * mm});
            skLineSegment(sketch, "E16.38.18.0", {"start": v(27.44, 2.01) * mm, "end": v(27.47, 1.8) * mm});
            skArc(sketch, "E16.41.18.0", {"start": v(27.44, 2.01) * mm, "mid": v(27.43, 2.04) * mm, "end": v(27.41, 2.07) * mm});
            skArc(sketch, "E16.45.18.0", {"start": v(27.45, 1.53) * mm, "mid": v(27.47, 1.55) * mm, "end": v(27.47, 1.58) * mm});
            skLineSegment(sketch, "E16.49.18.0", {"start": v(27.47, 1.58) * mm, "end": v(27.47, 1.8) * mm});
            skArc(sketch, "E16.4.19.0", {"start": v(23.97, 6.42) * mm, "mid": v(23.04, 5.73) * mm, "end": v(22.83, 4.58) * mm});
            skArc(sketch, "E16.8.19.0", {"start": v(24.58, 6.73) * mm, "mid": v(25.44, 7.58) * mm, "end": v(26.12, 8.58) * mm});
            skArc(sketch, "E16.9.19.0", {"start": v(23.6, 9.62) * mm, "mid": v(24.8, 9.47) * mm, "end": v(25.94, 9.1) * mm});
            skPoint(sketch, "E16.12.19.0", {"position": v(24.29, 6.5) * mm});
            skPoint(sketch, "E16.13.19.0", {"position": v(23.23, 9.62) * mm});
            skPoint(sketch, "E16.14.19.0", {"position": v(25.98, 9.08) * mm});
            skPoint(sketch, "E16.15.19.0", {"position": v(26.14, 8.6) * mm});
            skArc(sketch, "E16.16.19.0", {"start": v(20.9, 10.27) * mm, "mid": v(21.76, 9.48) * mm, "end": v(22.93, 9.5) * mm});
            skArc(sketch, "E16.20.19.0", {"start": v(21.44, 9.07) * mm, "mid": v(21.54, 8.98) * mm, "end": v(21.67, 8.98) * mm});
            skArc(sketch, "E16.24.19.0", {"start": v(23.98, 6.43) * mm, "mid": v(24.3, 6.55) * mm, "end": v(24.58, 6.73) * mm});
            skArc(sketch, "E16.28.19.0", {"start": v(23.6, 9.62) * mm, "mid": v(23.26, 9.6) * mm, "end": v(22.94, 9.5) * mm});
            skLineSegment(sketch, "E16.32.19.0", {"start": v(22.94, 9.5) * mm, "end": v(22.93, 9.5) * mm});
            skLineSegment(sketch, "E16.35.19.0", {"start": v(23.98, 6.43) * mm, "end": v(23.97, 6.42) * mm});
            skLineSegment(sketch, "E16.38.19.0", {"start": v(25.99, 9.05) * mm, "end": v(26.07, 8.85) * mm});
            skArc(sketch, "E16.41.19.0", {"start": v(25.99, 9.05) * mm, "mid": v(25.97, 9.08) * mm, "end": v(25.94, 9.1) * mm});
            skArc(sketch, "E16.45.19.0", {"start": v(26.12, 8.58) * mm, "mid": v(26.13, 8.6) * mm, "end": v(26.13, 8.64) * mm});
            skLineSegment(sketch, "E16.49.19.0", {"start": v(26.13, 8.64) * mm, "end": v(26.07, 8.85) * mm});
            skArc(sketch, "E16.4.20.0", {"start": v(21.5, 12.41) * mm, "mid": v(20.77, 11.5) * mm, "end": v(20.87, 10.33) * mm});
            skArc(sketch, "E16.8.20.0", {"start": v(22, 12.86) * mm, "mid": v(22.6, 13.9) * mm, "end": v(23, 15.05) * mm});
            skArc(sketch, "E16.9.20.0", {"start": v(20.3, 15.4) * mm, "mid": v(21.5, 15.57) * mm, "end": v(22.7, 15.5) * mm});
            skPoint(sketch, "E16.12.20.0", {"position": v(21.78, 12.57) * mm});
            skPoint(sketch, "E16.13.20.0", {"position": v(19.95, 15.3) * mm});
            skPoint(sketch, "E16.14.20.0", {"position": v(22.74, 15.5) * mm});
            skPoint(sketch, "E16.15.20.0", {"position": v(23.02, 15.08) * mm});
            skArc(sketch, "E16.16.20.0", {"start": v(17.53, 15.32) * mm, "mid": v(18.57, 14.79) * mm, "end": v(19.7, 15.1) * mm});
            skArc(sketch, "E16.20.20.0", {"start": v(18.36, 14.31) * mm, "mid": v(18.48, 14.25) * mm, "end": v(18.61, 14.28) * mm});
            skArc(sketch, "E16.24.20.0", {"start": v(21.5, 12.42) * mm, "mid": v(21.77, 12.61) * mm, "end": v(22, 12.86) * mm});
            skArc(sketch, "E16.28.20.0", {"start": v(20.3, 15.4) * mm, "mid": v(19.99, 15.3) * mm, "end": v(19.7, 15.12) * mm});
            skLineSegment(sketch, "E16.32.20.0", {"start": v(19.7, 15.12) * mm, "end": v(19.7, 15.1) * mm});
            skLineSegment(sketch, "E16.35.20.0", {"start": v(21.5, 12.42) * mm, "end": v(21.5, 12.41) * mm});
            skLineSegment(sketch, "E16.38.20.0", {"start": v(22.76, 15.47) * mm, "end": v(22.9, 15.3) * mm});
            skArc(sketch, "E16.41.20.0", {"start": v(22.76, 15.47) * mm, "mid": v(22.74, 15.49) * mm, "end": v(22.7, 15.5) * mm});
            skArc(sketch, "E16.45.20.0", {"start": v(23, 15.05) * mm, "mid": v(23.01, 15.08) * mm, "end": v(23, 15.1) * mm});
            skLineSegment(sketch, "E16.49.20.0", {"start": v(23, 15.1) * mm, "end": v(22.9, 15.3) * mm});
            skArc(sketch, "E16.4.21.0", {"start": v(17.55, 17.55) * mm, "mid": v(17.09, 16.48) * mm, "end": v(17.48, 15.38) * mm});
            skArc(sketch, "E16.8.21.0", {"start": v(17.92, 18.12) * mm, "mid": v(18.24, 19.29) * mm, "end": v(18.33, 20.5) * mm});
            skArc(sketch, "E16.9.21.0", {"start": v(15.62, 20.13) * mm, "mid": v(16.74, 20.6) * mm, "end": v(17.92, 20.85) * mm});
            skPoint(sketch, "E16.12.21.0", {"position": v(17.78, 17.78) * mm});
            skPoint(sketch, "E16.13.21.0", {"position": v(15.3, 19.95) * mm});
            skPoint(sketch, "E16.14.21.0", {"position": v(17.96, 20.85) * mm});
            skPoint(sketch, "E16.15.21.0", {"position": v(18.33, 20.52) * mm});
            skArc(sketch, "E16.16.21.0", {"start": v(12.97, 19.34) * mm, "mid": v(14.1, 19.1) * mm, "end": v(15.1, 19.7) * mm});
            skArc(sketch, "E16.20.21.0", {"start": v(14.03, 18.58) * mm, "mid": v(14.16, 18.54) * mm, "end": v(14.28, 18.61) * mm});
            skArc(sketch, "E16.24.21.0", {"start": v(17.56, 17.56) * mm, "mid": v(17.77, 17.82) * mm, "end": v(17.92, 18.12) * mm});
            skArc(sketch, "E16.28.21.0", {"start": v(15.62, 20.13) * mm, "mid": v(15.35, 19.94) * mm, "end": v(15.12, 19.7) * mm});
            skLineSegment(sketch, "E16.32.21.0", {"start": v(15.12, 19.7) * mm, "end": v(15.1, 19.7) * mm});
            skLineSegment(sketch, "E16.35.21.0", {"start": v(17.56, 17.56) * mm, "end": v(17.55, 17.55) * mm});
            skLineSegment(sketch, "E16.38.21.0", {"start": v(17.98, 20.83) * mm, "end": v(18.15, 20.7) * mm});
            skArc(sketch, "E16.41.21.0", {"start": v(17.98, 20.83) * mm, "mid": v(17.95, 20.85) * mm, "end": v(17.92, 20.85) * mm});
            skArc(sketch, "E16.45.21.0", {"start": v(18.33, 20.5) * mm, "mid": v(18.32, 20.52) * mm, "end": v(18.3, 20.54) * mm});
            skLineSegment(sketch, "E16.49.21.0", {"start": v(18.3, 20.54) * mm, "end": v(18.15, 20.7) * mm});
            skArc(sketch, "E16.4.22.0", {"start": v(12.41, 21.5) * mm, "mid": v(12.24, 20.34) * mm, "end": v(12.9, 19.38) * mm});
            skArc(sketch, "E16.8.22.0", {"start": v(12.62, 22.14) * mm, "mid": v(12.63, 23.35) * mm, "end": v(12.4, 24.54) * mm});
            skArc(sketch, "E16.9.22.0", {"start": v(9.88, 23.49) * mm, "mid": v(10.84, 24.23) * mm, "end": v(11.92, 24.78) * mm});
            skPoint(sketch, "E16.12.22.0", {"position": v(12.57, 21.78) * mm});
            skPoint(sketch, "E16.13.22.0", {"position": v(9.62, 23.23) * mm});
            skPoint(sketch, "E16.14.22.0", {"position": v(11.95, 24.79) * mm});
            skPoint(sketch, "E16.15.22.0", {"position": v(12.4, 24.57) * mm});
            skArc(sketch, "E16.16.22.0", {"start": v(7.52, 22.04) * mm, "mid": v(8.69, 22.1) * mm, "end": v(9.5, 22.93) * mm});
            skArc(sketch, "E16.20.22.0", {"start": v(8.75, 21.58) * mm, "mid": v(8.88, 21.58) * mm, "end": v(8.98, 21.67) * mm});
            skArc(sketch, "E16.24.22.0", {"start": v(12.42, 21.5) * mm, "mid": v(12.55, 21.81) * mm, "end": v(12.62, 22.14) * mm});
            skArc(sketch, "E16.28.22.0", {"start": v(9.88, 23.49) * mm, "mid": v(9.66, 23.23) * mm, "end": v(9.5, 22.94) * mm});
            skLineSegment(sketch, "E16.32.22.0", {"start": v(9.5, 22.94) * mm, "end": v(9.5, 22.93) * mm});
            skLineSegment(sketch, "E16.35.22.0", {"start": v(12.42, 21.5) * mm, "end": v(12.41, 21.5) * mm});
            skLineSegment(sketch, "E16.38.22.0", {"start": v(11.98, 24.78) * mm, "end": v(12.18, 24.7) * mm});
            skArc(sketch, "E16.41.22.0", {"start": v(11.98, 24.78) * mm, "mid": v(11.95, 24.78) * mm, "end": v(11.92, 24.78) * mm});
            skArc(sketch, "E16.45.22.0", {"start": v(12.4, 24.54) * mm, "mid": v(12.39, 24.56) * mm, "end": v(12.37, 24.58) * mm});
            skLineSegment(sketch, "E16.49.22.0", {"start": v(12.37, 24.58) * mm, "end": v(12.18, 24.7) * mm});
            skArc(sketch, "E16.4.23.0", {"start": v(6.42, 23.97) * mm, "mid": v(6.56, 22.81) * mm, "end": v(7.45, 22.06) * mm});
            skArc(sketch, "E16.8.23.0", {"start": v(6.46, 24.65) * mm, "mid": v(6.15, 25.82) * mm, "end": v(5.63, 26.91) * mm});
            skArc(sketch, "E16.9.23.0", {"start": v(3.47, 25.25) * mm, "mid": v(4.2, 26.2) * mm, "end": v(5.1, 27.02) * mm});
            skPoint(sketch, "E16.12.23.0", {"position": v(6.5, 24.29) * mm});
            skPoint(sketch, "E16.13.23.0", {"position": v(3.28, 24.93) * mm});
            skPoint(sketch, "E16.14.23.0", {"position": v(5.12, 27.04) * mm});
            skPoint(sketch, "E16.15.23.0", {"position": v(5.61, 26.94) * mm});
            skArc(sketch, "E16.16.23.0", {"start": v(1.56, 23.23) * mm, "mid": v(2.67, 23.59) * mm, "end": v(3.24, 24.6) * mm});
            skArc(sketch, "E16.20.23.0", {"start": v(2.86, 23.1) * mm, "mid": v(3, 23.14) * mm, "end": v(3.06, 23.26) * mm});
            skArc(sketch, "E16.24.23.0", {"start": v(6.43, 23.98) * mm, "mid": v(6.48, 24.32) * mm, "end": v(6.46, 24.65) * mm});
            skArc(sketch, "E16.28.23.0", {"start": v(3.47, 25.25) * mm, "mid": v(3.32, 24.94) * mm, "end": v(3.24, 24.62) * mm});
            skLineSegment(sketch, "E16.32.23.0", {"start": v(3.24, 24.62) * mm, "end": v(3.24, 24.6) * mm});
            skLineSegment(sketch, "E16.35.23.0", {"start": v(6.43, 23.98) * mm, "end": v(6.42, 23.97) * mm});
            skLineSegment(sketch, "E16.38.23.0", {"start": v(5.16, 27.03) * mm, "end": v(5.37, 27) * mm});
            skArc(sketch, "E16.41.23.0", {"start": v(5.16, 27.03) * mm, "mid": v(5.13, 27.03) * mm, "end": v(5.1, 27.02) * mm});
            skArc(sketch, "E16.45.23.0", {"start": v(5.63, 26.91) * mm, "mid": v(5.6, 26.93) * mm, "end": v(5.58, 26.95) * mm});
            skLineSegment(sketch, "E16.49.23.0", {"start": v(5.58, 26.95) * mm, "end": v(5.37, 27) * mm});
            skCircle(sketch, "E17", {"center": v(0, 0) * mm, "radius": 23.28 * mm});
            skSolve(sketch);
        }
        {
            var Q0;
            Q0 = qSketchRegion(id + "F3", true);
            extrude(context, id + "F4", {"entities" : qUnion([Q0]), "operationType" : NewBodyOperationType.ADD, "oppositeDirection" : true, "depth" : 6.35 * mm});
        }
        {
            var Q0;
            Q0=sQuery(id+"F3.wireOp",VERTEX,"E15.center");
            var Q1;
            Q1=makeQuery(id+"F1.opExtrude","SWEPT_BODY",BODY,{"disambiguationData":[OSD([sQuery(id+"F0.wireOp",EDGE,"E0")])]});
            hole(context, id + "F5", {"style" : HoleStyle.SIMPLE, "endStyle" : HoleEndStyle.THROUGH, "holeDiameter" : 12.7 * mm, "tappedDepth" : 12.7 * mm, "tapClearance" : 3, "locations" : qUnion([Q0]), "scope" : qUnion([Q1])});
        }
    });
